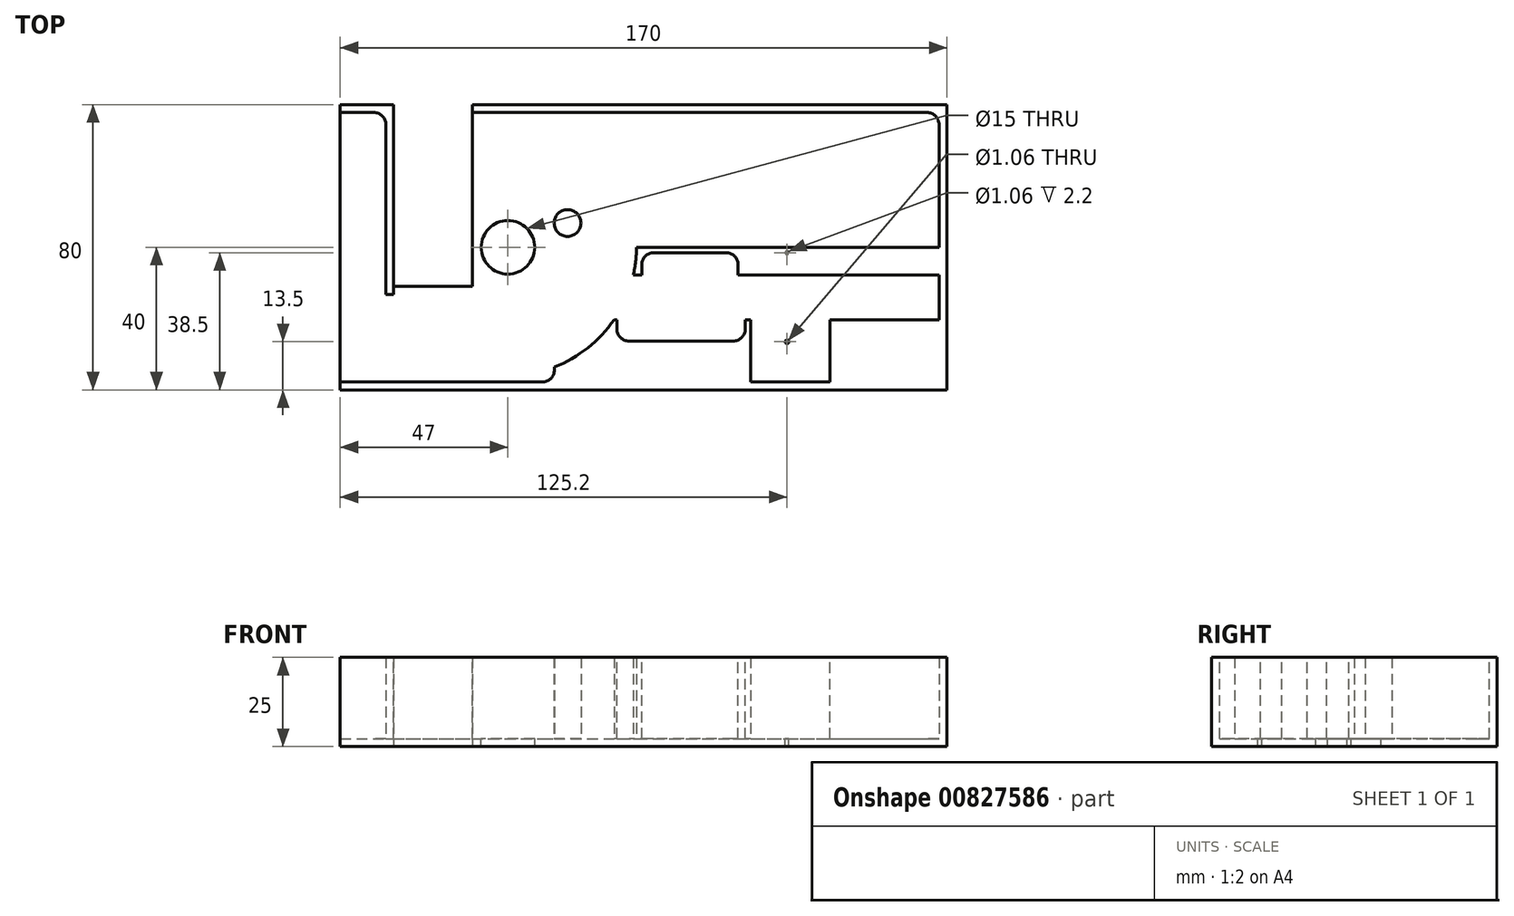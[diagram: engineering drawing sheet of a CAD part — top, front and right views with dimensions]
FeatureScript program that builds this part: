
annotation { "Feature Type Name" : "Feature", "Feature Type Description" : "" }
export const myFeature = defineFeature(function(context is Context, id is Id, definition is map)
    precondition{}
    {
        {
            var Q0;
            Q0=qCreatedBy(makeId("Top.planeOp"),FACE);
            var sketch = newSketch(context, id + "F0", { "sketchPlane" : qUnion([Q0])});
            skLineSegment(sketch, "E0.bottom", {"start": v(-85, 40) * mm, "end": v(85, 40) * mm});
            skLineSegment(sketch, "E0.top", {"start": v(-85, -40) * mm, "end": v(85, -40) * mm});
            skLineSegment(sketch, "E0.left", {"start": v(-85, 40) * mm, "end": v(-85, -40) * mm});
            skLineSegment(sketch, "E0.right", {"start": v(85, 40) * mm, "end": v(85, -40) * mm});
            skPoint(sketch, "E0.middle", {"position": v(0, 0) * mm});
            skLineSegment(sketch, "E1.bottom", {"start": v(-70, 40) * mm, "end": v(-48, 40) * mm});
            skLineSegment(sketch, "E1.top", {"start": v(-70, -11) * mm, "end": v(-48, -11) * mm});
            skLineSegment(sketch, "E1.left", {"start": v(-70, 40) * mm, "end": v(-70, -11) * mm});
            skLineSegment(sketch, "E1.right", {"start": v(-48, 40) * mm, "end": v(-48, -11) * mm});
            skSolve(sketch);
        }
        {
            var Q0;
            Q0=makeQuery(id+"F0.imprint","IMPRINT",FACE,{"disambiguationData":[TD([[makeQuery(id+"F0.imprint","IMPRINT",EDGE,{"derivedFrom":sQuery(id+"F0.wireOp",EDGE,"E0.top")}),1.0]])]});
            extrude(context, id + "F1", {"entities" : qUnion([Q0]), "depth" : 25 * mm, "offsetDistance" : 25 * mm});
        }
        {
            var Q0;
            Q0=makeQuery(id+"F1.opExtrude","CAP_FACE",FACE,{"disambiguationData":[OSD([sQuery(id+"F0.wireOp",EDGE,"E0.bottom"),sQuery(id+"F0.wireOp",EDGE,"E0.top"),sQuery(id+"F0.wireOp",EDGE,"E0.left"),sQuery(id+"F0.wireOp",EDGE,"E0.right"),sQuery(id+"F0.wireOp",EDGE,"E1.top"),sQuery(id+"F0.wireOp",EDGE,"E1.left"),sQuery(id+"F0.wireOp",EDGE,"E1.right")])],"isStart":false});
            shell(context, id + "F2", {"entities" : qUnion([Q0]), "thickness" : 2.2 * mm});
        }
        {
            var Q0;
            Q0=makeQuery(id+"F2.opShell","OFFSET_FACE",FACE,{"disambiguationData":[OSD([sQuery(id+"F0.wireOp",EDGE,"E0.bottom"),sQuery(id+"F0.wireOp",EDGE,"E0.top"),sQuery(id+"F0.wireOp",EDGE,"E0.left"),sQuery(id+"F0.wireOp",EDGE,"E0.right"),sQuery(id+"F0.wireOp",EDGE,"E1.top"),sQuery(id+"F0.wireOp",EDGE,"E1.left"),sQuery(id+"F0.wireOp",EDGE,"E1.right")])]});
            var sketch = newSketch(context, id + "F3", { "sketchPlane" : qUnion([Q0])});
            skCircle(sketch, "E2.0", {"center": v(-38, 0) * mm, "radius": 7.5 * mm});
            skSolve(sketch);
        }
        {
            var Q0;
            Q0 = qSketchRegion(id + "F3", true);
            extrude(context, id + "F4", {"entities" : qUnion([Q0]), "operationType" : NewBodyOperationType.REMOVE, "oppositeDirection" : true, "depth" : 25 * mm, "offsetDistance" : 25 * mm});
        }
        {
            var Q0;
            Q0=makeQuery(id+"F2.opShell","OFFSET_FACE",FACE,{"disambiguationData":[OSD([sQuery(id+"F0.wireOp",EDGE,"E0.bottom"),sQuery(id+"F0.wireOp",EDGE,"E0.top"),sQuery(id+"F0.wireOp",EDGE,"E0.left"),sQuery(id+"F0.wireOp",EDGE,"E0.right"),sQuery(id+"F0.wireOp",EDGE,"E1.top"),sQuery(id+"F0.wireOp",EDGE,"E1.left"),sQuery(id+"F0.wireOp",EDGE,"E1.right")])]});
            var sketch = newSketch(context, id + "F5", { "sketchPlane" : qUnion([Q0])});
            skCircle(sketch, "E3", {"center": v(-21.3, 6.8) * mm, "radius": 3.75 * mm});
            skSolve(sketch);
        }
        {
            var Q0;
            Q0 = qSketchRegion(id + "F5", true);
            var Q1;
            Q1=makeQuery(id+"F1.opExtrude","CAP_FACE",FACE,{"disambiguationData":[OSD([sQuery(id+"F0.wireOp",EDGE,"E0.bottom"),sQuery(id+"F0.wireOp",EDGE,"E0.top"),sQuery(id+"F0.wireOp",EDGE,"E0.left"),sQuery(id+"F0.wireOp",EDGE,"E0.right"),sQuery(id+"F0.wireOp",EDGE,"E1.top"),sQuery(id+"F0.wireOp",EDGE,"E1.left"),sQuery(id+"F0.wireOp",EDGE,"E1.right")])],"isStart":false});
            extrude(context, id + "F6", {"entities" : qUnion([Q0]), "operationType" : NewBodyOperationType.ADD, "endBound" : BoundingType.UP_TO_SURFACE, "depth" : 25 * mm, "endBoundEntityFace" : qUnion([Q1]), "offsetDistance" : 25 * mm});
        }
        {
            var Q0;
            Q0=makeQuery(id+"F2.opShell","OFFSET_FACE",FACE,{"disambiguationData":[OSD([sQuery(id+"F0.wireOp",EDGE,"E0.bottom"),sQuery(id+"F0.wireOp",EDGE,"E0.top"),sQuery(id+"F0.wireOp",EDGE,"E0.left"),sQuery(id+"F0.wireOp",EDGE,"E0.right"),sQuery(id+"F0.wireOp",EDGE,"E1.top"),sQuery(id+"F0.wireOp",EDGE,"E1.left"),sQuery(id+"F0.wireOp",EDGE,"E1.right")])]});
            var sketch = newSketch(context, id + "F7", { "sketchPlane" : qUnion([Q0])});
            skLineSegment(sketch, "E4.bottom", {"start": v(-5, 0) * mm, "end": v(30, 0) * mm});
            skLineSegment(sketch, "E4.top", {"start": v(-5, -7.8) * mm, "end": v(30, -7.8) * mm});
            skLineSegment(sketch, "E4.left", {"start": v(-5, 0) * mm, "end": v(-5, -7.8) * mm});
            skLineSegment(sketch, "E4.right", {"start": v(30, 0) * mm, "end": v(30, -7.8) * mm});
            skLineSegment(sketch, "E5.bottom", {"start": v(30, -20.3) * mm, "end": v(-5, -20.3) * mm});
            skLineSegment(sketch, "E5.top", {"start": v(30, -37.8) * mm, "end": v(-5, -37.8) * mm});
            skLineSegment(sketch, "E5.left", {"start": v(30, -20.3) * mm, "end": v(30, -37.8) * mm});
            skLineSegment(sketch, "E5.right", {"start": v(-5, -20.3) * mm, "end": v(-5, -37.8) * mm});
            skLineSegment(sketch, "E6", {"start": v(-5, -20.3) * mm, "end": v(-8.27, -20.3) * mm});
            skCircle(sketch, "E7", {"center": v(-38, 0) * mm, "radius": 36 * mm});
            skLineSegment(sketch, "E8", {"start": v(-25, -33.57) * mm, "end": v(-25, -37.8) * mm});
            skCircle(sketch, "E9.0", {"center": v(40.5, -1.8) * mm, "radius": 12.5 * mm});
            skSolve(sketch);
        }
        {
            var Q0;
            Q0=makeQuery(id+"F7.imprint","IMPRINT",FACE,{"disambiguationData":[TD([[makeQuery(id+"F7.imprint","IMPRINT",EDGE,{"derivedFrom":sQuery(id+"F7.wireOp",EDGE,"E5.bottom")}),1.0]])]});
            var Q1;
            {var subQ3=sQuery(id+"F7.wireOp",EDGE,"E5.right");Q1=makeQuery(id+"F7.imprint","IMPRINT",FACE,{"disambiguationData":[TD([[makeQuery(id+"F7.imprint","IMPRINT",EDGE,{"derivedFrom":subQ3}),-1.0]])]});}
            var Q2;
            {var subQ0=sQuery(id+"F7.wireOp",EDGE,"E7");var subQ1=sQuery(id+"F7.wireOp",EDGE,"E4.bottom");var subQ2=makeQuery(id+"F7.imprint","INTERSECT",VERTEX,{"derivedFrom":[subQ1,subQ0]});Q2=makeQuery(id+"F7.imprint","IMPRINT",FACE,{"disambiguationData":[TD([[makeQuery(id+"F7.imprint","IMPRINT",EDGE,{"disambiguationData":[TD([[subQ2,-1.0]])],"derivedFrom":subQ1}),-1.0]])]});}
            var Q3;
            Q3=makeQuery(id+"F1.opExtrude","CAP_FACE",FACE,{"disambiguationData":[OSD([sQuery(id+"F0.wireOp",EDGE,"E0.bottom"),sQuery(id+"F0.wireOp",EDGE,"E0.top"),sQuery(id+"F0.wireOp",EDGE,"E0.left"),sQuery(id+"F0.wireOp",EDGE,"E0.right"),sQuery(id+"F0.wireOp",EDGE,"E1.top"),sQuery(id+"F0.wireOp",EDGE,"E1.left"),sQuery(id+"F0.wireOp",EDGE,"E1.right")])],"isStart":false});
            extrude(context, id + "F8", {"entities" : qUnion([Q0, Q1, Q2]), "operationType" : NewBodyOperationType.ADD, "endBound" : BoundingType.UP_TO_SURFACE, "depth" : 25 * mm, "endBoundEntityFace" : qUnion([Q3]), "offsetDistance" : 25 * mm});
        }
        {
            var Q0;
            {var subQ0=sQuery(id+"F0.wireOp",EDGE,"E0.top");Q0=makeQuery(id+"F8.boolean.opBoolean","MERGE",FACE,{"derivedFrom":[makeQuery(id+"F1.opExtrude","CAP_FACE",FACE,{"disambiguationData":[OSD([sQuery(id+"F0.wireOp",EDGE,"E0.bottom"),subQ0,sQuery(id+"F0.wireOp",EDGE,"E0.left"),sQuery(id+"F0.wireOp",EDGE,"E0.right"),sQuery(id+"F0.wireOp",EDGE,"E1.top"),sQuery(id+"F0.wireOp",EDGE,"E1.left"),sQuery(id+"F0.wireOp",EDGE,"E1.right")])],"isStart":false}),makeQuery(id+"F8.opExtrude","CAP_FACE",FACE,{"disambiguationData":[OSD([subQ0,sQuery(id+"F7.wireOp",EDGE,"E5.bottom"),sQuery(id+"F7.wireOp",EDGE,"E5.top"),sQuery(id+"F7.wireOp",EDGE,"E5.left"),sQuery(id+"F7.wireOp",EDGE,"E6"),sQuery(id+"F7.wireOp",EDGE,"E7"),sQuery(id+"F7.wireOp",EDGE,"E8")])],"isStart":false})]});}
            var sketch = newSketch(context, id + "F9", { "sketchPlane" : qUnion([Q0])});
            skLineSegment(sketch, "E10.bottom", {"start": v(-45.8, 37.8) * mm, "end": v(-70, 37.8) * mm});
            skLineSegment(sketch, "E10.top", {"start": v(-45.8, -13.2) * mm, "end": v(-70, -13.2) * mm});
            skLineSegment(sketch, "E10.left", {"start": v(-45.8, 37.8) * mm, "end": v(-45.8, -13.2) * mm});
            skLineSegment(sketch, "E10.right", {"start": v(-70, 37.8) * mm, "end": v(-70, -13.2) * mm});
            skSolve(sketch);
        }
        {
            var Q0;
            Q0 = qSketchRegion(id + "F9", true);
            var Q1;
            Q1=makeQuery(id+"F2.opShell","OFFSET_FACE",FACE,{"disambiguationData":[OSD([sQuery(id+"F0.wireOp",EDGE,"E0.bottom"),sQuery(id+"F0.wireOp",EDGE,"E0.top"),sQuery(id+"F0.wireOp",EDGE,"E0.left"),sQuery(id+"F0.wireOp",EDGE,"E0.right"),sQuery(id+"F0.wireOp",EDGE,"E1.top"),sQuery(id+"F0.wireOp",EDGE,"E1.left"),sQuery(id+"F0.wireOp",EDGE,"E1.right")])]});
            extrude(context, id + "F10", {"entities" : qUnion([Q0]), "operationType" : NewBodyOperationType.REMOVE, "endBound" : BoundingType.UP_TO_SURFACE, "oppositeDirection" : true, "depth" : 25 * mm, "endBoundEntityFace" : qUnion([Q1]), "offsetDistance" : 25 * mm});
        }
        {
            var Q0;
            Q0=makeQuery(id+"F8.opExtrude","CAP_FACE",FACE,{"disambiguationData":[OSD([sQuery(id+"F7.wireOp",EDGE,"E4.bottom"),sQuery(id+"F7.wireOp",EDGE,"E4.top"),sQuery(id+"F7.wireOp",EDGE,"E7"),sQuery(id+"F7.wireOp",EDGE,"E9.0")])],"isStart":false});
            var sketch = newSketch(context, id + "F11", { "sketchPlane" : qUnion([Q0])});
            skArc(sketch, "E11.0.0", {"start": v(29.53, -7.8) * mm, "mid": v(28.2, -4.01) * mm, "end": v(28.13, 0) * mm});
            skLineSegment(sketch, "E11.0.1", {"start": v(28.13, 0) * mm, "end": v(-2, 0) * mm});
            skArc(sketch, "E11.0.2", {"start": v(-2, 0) * mm, "mid": v(-2.21, -3.92) * mm, "end": v(-2.86, -7.8) * mm});
            skLineSegment(sketch, "E11.0.3", {"start": v(-2.86, -7.8) * mm, "end": v(29.53, -7.8) * mm});
            skLineSegment(sketch, "E12.0.0", {"start": v(-48, 40) * mm, "end": v(-48, 37.8) * mm});
            skLineSegment(sketch, "E12.0.1", {"start": v(-48, 37.8) * mm, "end": v(82.8, 37.8) * mm});
            skLineSegment(sketch, "E12.0.2", {"start": v(82.8, 37.8) * mm, "end": v(82.8, -37.8) * mm});
            skLineSegment(sketch, "E12.0.4", {"start": v(30, -37.8) * mm, "end": v(30, -20.3) * mm});
            skLineSegment(sketch, "E12.0.5", {"start": v(30, -20.3) * mm, "end": v(-8.27, -20.3) * mm});
            skArc(sketch, "E12.0.6", {"start": v(-8.27, -20.3) * mm, "mid": v(-15.63, -28.2) * mm, "end": v(-25, -33.57) * mm});
            skLineSegment(sketch, "E12.0.7", {"start": v(-25, -33.57) * mm, "end": v(-25, -37.8) * mm});
            skLineSegment(sketch, "E12.0.9", {"start": v(-82.8, -37.8) * mm, "end": v(-82.8, 37.8) * mm});
            skLineSegment(sketch, "E12.0.10", {"start": v(-82.8, 37.8) * mm, "end": v(-72.2, 37.8) * mm});
            skLineSegment(sketch, "E12.0.11", {"start": v(-72.2, 37.8) * mm, "end": v(-72.2, -13.2) * mm});
            skLineSegment(sketch, "E12.0.12", {"start": v(-72.2, -13.2) * mm, "end": v(-70, -13.2) * mm});
            skLineSegment(sketch, "E12.0.13", {"start": v(-70, -13.2) * mm, "end": v(-70, 40) * mm});
            skLineSegment(sketch, "E12.0.14", {"start": v(-70, 40) * mm, "end": v(-85, 40) * mm});
            skLineSegment(sketch, "E12.0.15", {"start": v(-85, 40) * mm, "end": v(-85, -40) * mm});
            skLineSegment(sketch, "E12.0.17", {"start": v(85, -40) * mm, "end": v(85, 40) * mm});
            skLineSegment(sketch, "E12.0.18", {"start": v(85, 40) * mm, "end": v(-48, 40) * mm});
            skArc(sketch, "E13.0", {"start": v(27.24, -6.3) * mm, "mid": v(26.66, -3.93) * mm, "end": v(26.5, -1.5) * mm});
            skLineSegment(sketch, "E13.1", {"start": v(-1.03, -6.3) * mm, "end": v(27.24, -6.3) * mm});
            skArc(sketch, "E13.2", {"start": v(-0.53, -1.5) * mm, "mid": v(-0.7, -3.9) * mm, "end": v(-1.03, -6.3) * mm});
            skLineSegment(sketch, "E13.3", {"start": v(26.5, -1.5) * mm, "end": v(-0.53, -1.5) * mm});
            skLineSegment(sketch, "E14", {"start": v(-25, -37.8) * mm, "end": v(-25, -40) * mm});
            skLineSegment(sketch, "E15", {"start": v(30, -37.8) * mm, "end": v(30, -40) * mm});
            skLineSegment(sketch, "E16.0", {"start": v(-25, -40) * mm, "end": v(30, -40) * mm});
            skLineSegment(sketch, "E17.0", {"start": v(-23.5, -37.5) * mm, "end": v(-23.5, -38.5) * mm});
            skLineSegment(sketch, "E17.1", {"start": v(-23.5, -34.58) * mm, "end": v(-23.5, -37.5) * mm});
            skLineSegment(sketch, "E17.2", {"start": v(28.5, -37.5) * mm, "end": v(28.5, -38.5) * mm});
            skLineSegment(sketch, "E17.3", {"start": v(28.5, -37.5) * mm, "end": v(28.5, -21.8) * mm});
            skLineSegment(sketch, "E17.4", {"start": v(28.5, -21.8) * mm, "end": v(-7.49, -21.8) * mm});
            skLineSegment(sketch, "E17.5", {"start": v(-23.5, -38.5) * mm, "end": v(28.5, -38.5) * mm});
            skArc(sketch, "E17.6", {"start": v(-7.49, -21.8) * mm, "mid": v(-14.6, -29.3) * mm, "end": v(-23.5, -34.58) * mm});
            skLineSegment(sketch, "E18", {"start": v(-0.53, -1.5) * mm, "end": v(-0.53, -21.8) * mm});
            skLineSegment(sketch, "E19", {"start": v(-7.49, -21.8) * mm, "end": v(-7.49, -26.3) * mm});
            skLineSegment(sketch, "E20", {"start": v(-7.49, -26.3) * mm, "end": v(28.5, -26.3) * mm});
            skLineSegment(sketch, "E21", {"start": v(26.5, -1.5) * mm, "end": v(26.5, -21.8) * mm});
            skLineSegment(sketch, "E22", {"start": v(-7.49, -21.8) * mm, "end": v(-7.49, -20.3) * mm});
            skLineSegment(sketch, "E23", {"start": v(28.5, -21.8) * mm, "end": v(28.5, -20.3) * mm});
            skSolve(sketch);
        }
        {
            var Q0;
            {var subQ5=sQuery(id+"F11.wireOp",EDGE,"E13.3");Q0=makeQuery(id+"F11.imprint","IMPRINT",FACE,{"disambiguationData":[TD([[makeQuery(id+"F11.imprint","IMPRINT",EDGE,{"derivedFrom":subQ5}),1.0]])]});}
            var Q1;
            {var subQ0=sQuery(id+"F11.wireOp",EDGE,"E18");var subQ1=sQuery(id+"F11.wireOp",EDGE,"E11.0.3");var subQ2=makeQuery(id+"F11.imprint","INTERSECT",VERTEX,{"derivedFrom":[subQ1,subQ0]});Q1=makeQuery(id+"F11.imprint","IMPRINT",FACE,{"disambiguationData":[TD([[makeQuery(id+"F11.imprint","IMPRINT",EDGE,{"disambiguationData":[TD([[subQ2,-1.0]])],"derivedFrom":subQ1}),1.0]])]});}
            var Q2;
            {var subQ0=sQuery(id+"F11.wireOp",EDGE,"E21");var subQ1=sQuery(id+"F11.wireOp",EDGE,"E12.0.5");var subQ2=makeQuery(id+"F11.imprint","INTERSECT",VERTEX,{"derivedFrom":[subQ1,subQ0]});Q2=makeQuery(id+"F11.imprint","IMPRINT",FACE,{"disambiguationData":[TD([[makeQuery(id+"F11.imprint","IMPRINT",EDGE,{"disambiguationData":[TD([[subQ2,-1.0]])],"derivedFrom":subQ1}),1.0]])]});}
            var Q3;
            {var subQ0=sQuery(id+"F11.wireOp",EDGE,"E19");Q3=makeQuery(id+"F11.imprint","IMPRINT",FACE,{"disambiguationData":[TD([[makeQuery(id+"F11.imprint","IMPRINT",EDGE,{"derivedFrom":subQ0}),1.0]])]});}
            var Q4;
            {var subQ0=sQuery(id+"F11.wireOp",EDGE,"E22");Q4=makeQuery(id+"F11.imprint","IMPRINT",FACE,{"disambiguationData":[TD([[makeQuery(id+"F11.imprint","IMPRINT",EDGE,{"derivedFrom":subQ0}),-1.0]])]});}
            var Q5;
            {var subQ0=sQuery(id+"F11.wireOp",EDGE,"E23");Q5=makeQuery(id+"F11.imprint","IMPRINT",FACE,{"disambiguationData":[TD([[makeQuery(id+"F11.imprint","IMPRINT",EDGE,{"derivedFrom":subQ0}),1.0]])]});}
            var Q6;
            Q6=makeQuery(id+"F10.boolean.opBoolean","MERGE",FACE,{"derivedFrom":[makeQuery(id+"F2.opShell","OFFSET_FACE",FACE,{"disambiguationData":[OSD([sQuery(id+"F0.wireOp",EDGE,"E0.bottom"),sQuery(id+"F0.wireOp",EDGE,"E0.top"),sQuery(id+"F0.wireOp",EDGE,"E0.left"),sQuery(id+"F0.wireOp",EDGE,"E0.right"),sQuery(id+"F0.wireOp",EDGE,"E1.top"),sQuery(id+"F0.wireOp",EDGE,"E1.left"),sQuery(id+"F0.wireOp",EDGE,"E1.right")])]})],"fromTools":[makeQuery(id+"F10.opExtrude","CAP_FACE",FACE,{"disambiguationData":[OSD([sQuery(id+"F9.wireOp",EDGE,"E10.bottom"),sQuery(id+"F9.wireOp",EDGE,"E10.top"),sQuery(id+"F9.wireOp",EDGE,"E10.left"),sQuery(id+"F9.wireOp",EDGE,"E10.right")])],"isStart":false})]});
            extrude(context, id + "F12", {"entities" : qUnion([Q0, Q1, Q2, Q3, Q4, Q5]), "operationType" : NewBodyOperationType.REMOVE, "endBound" : BoundingType.UP_TO_SURFACE, "oppositeDirection" : true, "depth" : 25 * mm, "endBoundEntityFace" : qUnion([Q6]), "offsetDistance" : 25 * mm});
        }
        {
            var Q0;
            Q0=makeQuery(id+"F12.boolean.opBoolean","COPY",EDGE,{"derivedFrom":makeQuery(id+"F12.opExtrude","SWEPT_EDGE",EDGE,{"disambiguationData":[OSD([sQuery(id+"F11.wireOp",EDGE,"E13.2"),sQuery(id+"F11.wireOp",EDGE,"E13.3"),sQuery(id+"F11.wireOp",EDGE,"E18")])]})});
            var Q1;
            Q1=makeQuery(id+"F12.boolean.opBoolean","COPY",EDGE,{"derivedFrom":makeQuery(id+"F12.opExtrude","SWEPT_EDGE",EDGE,{"disambiguationData":[OSD([sQuery(id+"F11.wireOp",EDGE,"E13.0"),sQuery(id+"F11.wireOp",EDGE,"E13.3"),sQuery(id+"F11.wireOp",EDGE,"E21")])]})});
            var Q2;
            Q2=makeQuery(id+"F12.boolean.opBoolean","COPY",EDGE,{"derivedFrom":makeQuery(id+"F12.opExtrude","SWEPT_EDGE",EDGE,{"disambiguationData":[OSD([sQuery(id+"F11.wireOp",EDGE,"E17.3"),sQuery(id+"F11.wireOp",EDGE,"E20")])]})});
            var Q3;
            Q3=makeQuery(id+"F12.boolean.opBoolean","COPY",EDGE,{"derivedFrom":makeQuery(id+"F12.opExtrude","SWEPT_EDGE",EDGE,{"disambiguationData":[OSD([sQuery(id+"F11.wireOp",EDGE,"E19"),sQuery(id+"F11.wireOp",EDGE,"E20")])]})});
            var Q4;
            Q4=makeQuery(id+"F8.opExtrude","SWEPT_EDGE",EDGE,{"disambiguationData":[OSD([sQuery(id+"F0.wireOp",EDGE,"E0.top"),sQuery(id+"F7.wireOp",EDGE,"E5.top"),sQuery(id+"F7.wireOp",EDGE,"E5.left")])]});
            var Q5;
            Q5=makeQuery(id+"F2.opShell","OFFSET_EDGE",EDGE,{"disambiguationData":[OSD([sQuery(id+"F0.wireOp",EDGE,"E0.top"),sQuery(id+"F0.wireOp",EDGE,"E0.right")])]});
            var Q6;
            Q6=makeQuery(id+"F2.opShell","OFFSET_EDGE",EDGE,{"disambiguationData":[OSD([sQuery(id+"F0.wireOp",EDGE,"E0.bottom"),sQuery(id+"F0.wireOp",EDGE,"E0.right")])]});
            var Q7;
            Q7=makeQuery(id+"F2.opShell","OFFSET_EDGE",EDGE,{"disambiguationData":[OSD([sQuery(id+"F0.wireOp",EDGE,"E0.bottom"),sQuery(id+"F0.wireOp",EDGE,"E1.left")])]});
            var Q8;
            Q8=makeQuery(id+"F2.opShell","OFFSET_EDGE",EDGE,{"disambiguationData":[OSD([sQuery(id+"F0.wireOp",EDGE,"E0.bottom"),sQuery(id+"F0.wireOp",EDGE,"E0.left")])]});
            var Q9;
            Q9=makeQuery(id+"F2.opShell","OFFSET_EDGE",EDGE,{"disambiguationData":[OSD([sQuery(id+"F0.wireOp",EDGE,"E0.top"),sQuery(id+"F0.wireOp",EDGE,"E0.left")])]});
            var Q10;
            Q10=makeQuery(id+"F8.opExtrude","SWEPT_EDGE",EDGE,{"disambiguationData":[OSD([sQuery(id+"F0.wireOp",EDGE,"E0.top"),sQuery(id+"F7.wireOp",EDGE,"E8")])]});
            fillet(context, id + "F13", {"entities" : qUnion([Q0, Q1, Q2, Q3, Q4, Q5, Q6, Q7, Q8, Q9, Q10]), "radius" : 3.4 * mm, "tangentPropagation" : true, "allowEdgeOverflow" : false});
        }
        {
            var Q0;
            Q0=makeQuery(id+"F12.boolean.opBoolean","MERGE",FACE,{"derivedFrom":[makeQuery(id+"F10.boolean.opBoolean","MERGE",FACE,{"derivedFrom":[makeQuery(id+"F2.opShell","OFFSET_FACE",FACE,{"disambiguationData":[OSD([sQuery(id+"F0.wireOp",EDGE,"E0.bottom"),sQuery(id+"F0.wireOp",EDGE,"E0.top"),sQuery(id+"F0.wireOp",EDGE,"E0.left"),sQuery(id+"F0.wireOp",EDGE,"E0.right"),sQuery(id+"F0.wireOp",EDGE,"E1.top"),sQuery(id+"F0.wireOp",EDGE,"E1.left"),sQuery(id+"F0.wireOp",EDGE,"E1.right")])]})],"fromTools":[makeQuery(id+"F10.opExtrude","CAP_FACE",FACE,{"disambiguationData":[OSD([sQuery(id+"F9.wireOp",EDGE,"E10.bottom"),sQuery(id+"F9.wireOp",EDGE,"E10.top"),sQuery(id+"F9.wireOp",EDGE,"E10.left"),sQuery(id+"F9.wireOp",EDGE,"E10.right")])],"isStart":false})]})],"fromTools":[makeQuery(id+"F12.opExtrude","CAP_FACE",FACE,{"disambiguationData":[OSD([sQuery(id+"F11.wireOp",EDGE,"E11.0.3"),sQuery(id+"F11.wireOp",EDGE,"E13.0"),sQuery(id+"F11.wireOp",EDGE,"E13.3"),sQuery(id+"F11.wireOp",EDGE,"E18"),sQuery(id+"F11.wireOp",EDGE,"E21")])],"isStart":false}),makeQuery(id+"F12.opExtrude","CAP_FACE",FACE,{"disambiguationData":[OSD([sQuery(id+"F11.wireOp",EDGE,"E12.0.5"),sQuery(id+"F11.wireOp",EDGE,"E17.3"),sQuery(id+"F11.wireOp",EDGE,"E19"),sQuery(id+"F11.wireOp",EDGE,"E20"),sQuery(id+"F11.wireOp",EDGE,"E22"),sQuery(id+"F11.wireOp",EDGE,"E23")])],"isStart":false})]});
            var sketch = newSketch(context, id + "F14", { "sketchPlane" : qUnion([Q0])});
            skCircle(sketch, "E24", {"center": v(40.2, -1.5) * mm, "radius": 0.53 * mm});
            skLineSegment(sketch, "E25", {"start": v(67.78, -14) * mm, "end": v(32.12, -14) * mm, "construction": true});
            skCircle(sketch, "E26.MirrorC", {"center": v(40.2, -26.5) * mm, "radius": 0.53 * mm});
            skSolve(sketch);
        }
        {
            var Q0;
            Q0 = qSketchRegion(id + "F14", true);
            extrude(context, id + "F15", {"entities" : qUnion([Q0]), "operationType" : NewBodyOperationType.REMOVE, "oppositeDirection" : true, "depth" : 25 * mm, "offsetDistance" : 25 * mm});
        }
        {
            var Q0;
            {var subQ0=sQuery(id+"F0.wireOp",EDGE,"E0.top");Q0=makeQuery(id+"F8.boolean.opBoolean","MERGE",FACE,{"derivedFrom":[makeQuery(id+"F1.opExtrude","CAP_FACE",FACE,{"disambiguationData":[OSD([sQuery(id+"F0.wireOp",EDGE,"E0.bottom"),subQ0,sQuery(id+"F0.wireOp",EDGE,"E0.left"),sQuery(id+"F0.wireOp",EDGE,"E0.right"),sQuery(id+"F0.wireOp",EDGE,"E1.top"),sQuery(id+"F0.wireOp",EDGE,"E1.left"),sQuery(id+"F0.wireOp",EDGE,"E1.right")])],"isStart":false}),makeQuery(id+"F8.opExtrude","CAP_FACE",FACE,{"disambiguationData":[OSD([subQ0,sQuery(id+"F7.wireOp",EDGE,"E5.bottom"),sQuery(id+"F7.wireOp",EDGE,"E5.top"),sQuery(id+"F7.wireOp",EDGE,"E5.left"),sQuery(id+"F7.wireOp",EDGE,"E6"),sQuery(id+"F7.wireOp",EDGE,"E7"),sQuery(id+"F7.wireOp",EDGE,"E8")])],"isStart":false})]});}
            var sketch = newSketch(context, id + "F16", { "sketchPlane" : qUnion([Q0])});
            skPoint(sketch, "E27.0", {"position": v(26.5, -7.8) * mm});
            skLineSegment(sketch, "E28.bottom", {"start": v(26.5, -7.8) * mm, "end": v(85, -7.8) * mm});
            skLineSegment(sketch, "E28.top", {"start": v(26.5, 0) * mm, "end": v(85, 0) * mm});
            skLineSegment(sketch, "E28.left", {"start": v(26.5, -7.8) * mm, "end": v(26.5, 0) * mm});
            skLineSegment(sketch, "E28.right", {"start": v(85, -7.8) * mm, "end": v(85, 0) * mm});
            skLineSegment(sketch, "E29.bottom", {"start": v(82.8, -20.3) * mm, "end": v(52.28, -20.3) * mm});
            skLineSegment(sketch, "E29.top", {"start": v(82.8, -37.8) * mm, "end": v(52.28, -37.8) * mm});
            skLineSegment(sketch, "E29.left", {"start": v(82.8, -20.3) * mm, "end": v(82.8, -37.8) * mm});
            skLineSegment(sketch, "E29.right", {"start": v(52.28, -20.3) * mm, "end": v(52.28, -37.8) * mm});
            skSolve(sketch);
        }
        {
            var Q0;
            Q0 = qSketchRegion(id + "F16", true);
            var Q1;
            Q1=makeQuery(id+"F12.boolean.opBoolean","MERGE",FACE,{"derivedFrom":[makeQuery(id+"F10.boolean.opBoolean","MERGE",FACE,{"derivedFrom":[makeQuery(id+"F2.opShell","OFFSET_FACE",FACE,{"disambiguationData":[OSD([sQuery(id+"F0.wireOp",EDGE,"E0.bottom"),sQuery(id+"F0.wireOp",EDGE,"E0.top"),sQuery(id+"F0.wireOp",EDGE,"E0.left"),sQuery(id+"F0.wireOp",EDGE,"E0.right"),sQuery(id+"F0.wireOp",EDGE,"E1.top"),sQuery(id+"F0.wireOp",EDGE,"E1.left"),sQuery(id+"F0.wireOp",EDGE,"E1.right")])]})],"fromTools":[makeQuery(id+"F10.opExtrude","CAP_FACE",FACE,{"disambiguationData":[OSD([sQuery(id+"F9.wireOp",EDGE,"E10.bottom"),sQuery(id+"F9.wireOp",EDGE,"E10.top"),sQuery(id+"F9.wireOp",EDGE,"E10.left"),sQuery(id+"F9.wireOp",EDGE,"E10.right")])],"isStart":false})]})],"fromTools":[makeQuery(id+"F12.opExtrude","CAP_FACE",FACE,{"disambiguationData":[OSD([sQuery(id+"F11.wireOp",EDGE,"E11.0.3"),sQuery(id+"F11.wireOp",EDGE,"E13.0"),sQuery(id+"F11.wireOp",EDGE,"E13.3"),sQuery(id+"F11.wireOp",EDGE,"E18"),sQuery(id+"F11.wireOp",EDGE,"E21")])],"isStart":false}),makeQuery(id+"F12.opExtrude","CAP_FACE",FACE,{"disambiguationData":[OSD([sQuery(id+"F11.wireOp",EDGE,"E12.0.5"),sQuery(id+"F11.wireOp",EDGE,"E17.3"),sQuery(id+"F11.wireOp",EDGE,"E19"),sQuery(id+"F11.wireOp",EDGE,"E20"),sQuery(id+"F11.wireOp",EDGE,"E22"),sQuery(id+"F11.wireOp",EDGE,"E23")])],"isStart":false})]});
            extrude(context, id + "F17", {"entities" : qUnion([Q0]), "operationType" : NewBodyOperationType.ADD, "endBound" : BoundingType.UP_TO_SURFACE, "oppositeDirection" : true, "depth" : 25 * mm, "endBoundEntityFace" : qUnion([Q1]), "offsetDistance" : 25 * mm});
        }
        {
            var Q0;
            {var subQ0=sQuery(id+"F7.wireOp",EDGE,"E7");var subQ1=sQuery(id+"F0.wireOp",EDGE,"E0.top");Q0=makeQuery(id+"F17.boolean.opBoolean","MERGE",FACE,{"derivedFrom":[makeQuery(id+"F8.opExtrude","CAP_FACE",FACE,{"disambiguationData":[OSD([sQuery(id+"F7.wireOp",EDGE,"E4.bottom"),sQuery(id+"F7.wireOp",EDGE,"E4.top"),subQ0,sQuery(id+"F7.wireOp",EDGE,"E9.0")])],"isStart":false}),makeQuery(id+"F8.boolean.opBoolean","MERGE",FACE,{"derivedFrom":[makeQuery(id+"F1.opExtrude","CAP_FACE",FACE,{"disambiguationData":[OSD([sQuery(id+"F0.wireOp",EDGE,"E0.bottom"),subQ1,sQuery(id+"F0.wireOp",EDGE,"E0.left"),sQuery(id+"F0.wireOp",EDGE,"E0.right"),sQuery(id+"F0.wireOp",EDGE,"E1.top"),sQuery(id+"F0.wireOp",EDGE,"E1.left"),sQuery(id+"F0.wireOp",EDGE,"E1.right")])],"isStart":false}),makeQuery(id+"F8.opExtrude","CAP_FACE",FACE,{"disambiguationData":[OSD([subQ1,sQuery(id+"F7.wireOp",EDGE,"E5.bottom"),sQuery(id+"F7.wireOp",EDGE,"E5.top"),sQuery(id+"F7.wireOp",EDGE,"E5.left"),sQuery(id+"F7.wireOp",EDGE,"E6"),subQ0,sQuery(id+"F7.wireOp",EDGE,"E8")])],"isStart":false})]}),makeQuery(id+"F17.opExtrude","CAP_FACE",FACE,{"disambiguationData":[OSD([sQuery(id+"F16.wireOp",EDGE,"E28.bottom"),sQuery(id+"F16.wireOp",EDGE,"E28.top"),sQuery(id+"F16.wireOp",EDGE,"E28.left"),sQuery(id+"F16.wireOp",EDGE,"E28.right")])],"isStart":true}),makeQuery(id+"F17.opExtrude","CAP_FACE",FACE,{"disambiguationData":[OSD([sQuery(id+"F16.wireOp",EDGE,"E29.bottom"),sQuery(id+"F16.wireOp",EDGE,"E29.top"),sQuery(id+"F16.wireOp",EDGE,"E29.left"),sQuery(id+"F16.wireOp",EDGE,"E29.right")])],"isStart":true})]});}
            var sketch = newSketch(context, id + "F18", { "sketchPlane" : qUnion([Q0])});
            skLineSegment(sketch, "E30.bottom", {"start": v(-79.4, 37.8) * mm, "end": v(-85, 37.8) * mm});
            skLineSegment(sketch, "E30.top", {"start": v(-79.4, -37.8) * mm, "end": v(-85, -37.8) * mm});
            skLineSegment(sketch, "E30.left", {"start": v(-79.4, 37.8) * mm, "end": v(-79.4, -37.8) * mm});
            skLineSegment(sketch, "E30.right", {"start": v(-85, 37.8) * mm, "end": v(-85, -37.8) * mm});
            skSolve(sketch);
        }
        {
            var Q0;
            Q0 = qSketchRegion(id + "F18", true);
            var Q1;
            Q1=makeQuery(id+"F12.boolean.opBoolean","MERGE",FACE,{"derivedFrom":[makeQuery(id+"F10.boolean.opBoolean","MERGE",FACE,{"derivedFrom":[makeQuery(id+"F2.opShell","OFFSET_FACE",FACE,{"disambiguationData":[OSD([sQuery(id+"F0.wireOp",EDGE,"E0.bottom"),sQuery(id+"F0.wireOp",EDGE,"E0.top"),sQuery(id+"F0.wireOp",EDGE,"E0.left"),sQuery(id+"F0.wireOp",EDGE,"E0.right"),sQuery(id+"F0.wireOp",EDGE,"E1.top"),sQuery(id+"F0.wireOp",EDGE,"E1.left"),sQuery(id+"F0.wireOp",EDGE,"E1.right")])]})],"fromTools":[makeQuery(id+"F10.opExtrude","CAP_FACE",FACE,{"disambiguationData":[OSD([sQuery(id+"F9.wireOp",EDGE,"E10.bottom"),sQuery(id+"F9.wireOp",EDGE,"E10.top"),sQuery(id+"F9.wireOp",EDGE,"E10.left"),sQuery(id+"F9.wireOp",EDGE,"E10.right")])],"isStart":false})]})],"fromTools":[makeQuery(id+"F12.opExtrude","CAP_FACE",FACE,{"disambiguationData":[OSD([sQuery(id+"F11.wireOp",EDGE,"E11.0.3"),sQuery(id+"F11.wireOp",EDGE,"E13.0"),sQuery(id+"F11.wireOp",EDGE,"E13.3"),sQuery(id+"F11.wireOp",EDGE,"E18"),sQuery(id+"F11.wireOp",EDGE,"E21")])],"isStart":false}),makeQuery(id+"F12.opExtrude","CAP_FACE",FACE,{"disambiguationData":[OSD([sQuery(id+"F11.wireOp",EDGE,"E12.0.5"),sQuery(id+"F11.wireOp",EDGE,"E17.3"),sQuery(id+"F11.wireOp",EDGE,"E19"),sQuery(id+"F11.wireOp",EDGE,"E20"),sQuery(id+"F11.wireOp",EDGE,"E22"),sQuery(id+"F11.wireOp",EDGE,"E23")])],"isStart":false})]});
            extrude(context, id + "F19", {"entities" : qUnion([Q0]), "operationType" : NewBodyOperationType.REMOVE, "endBound" : BoundingType.UP_TO_SURFACE, "oppositeDirection" : true, "depth" : 25 * mm, "endBoundEntityFace" : qUnion([Q1]), "offsetDistance" : 25 * mm});
        }
    });
